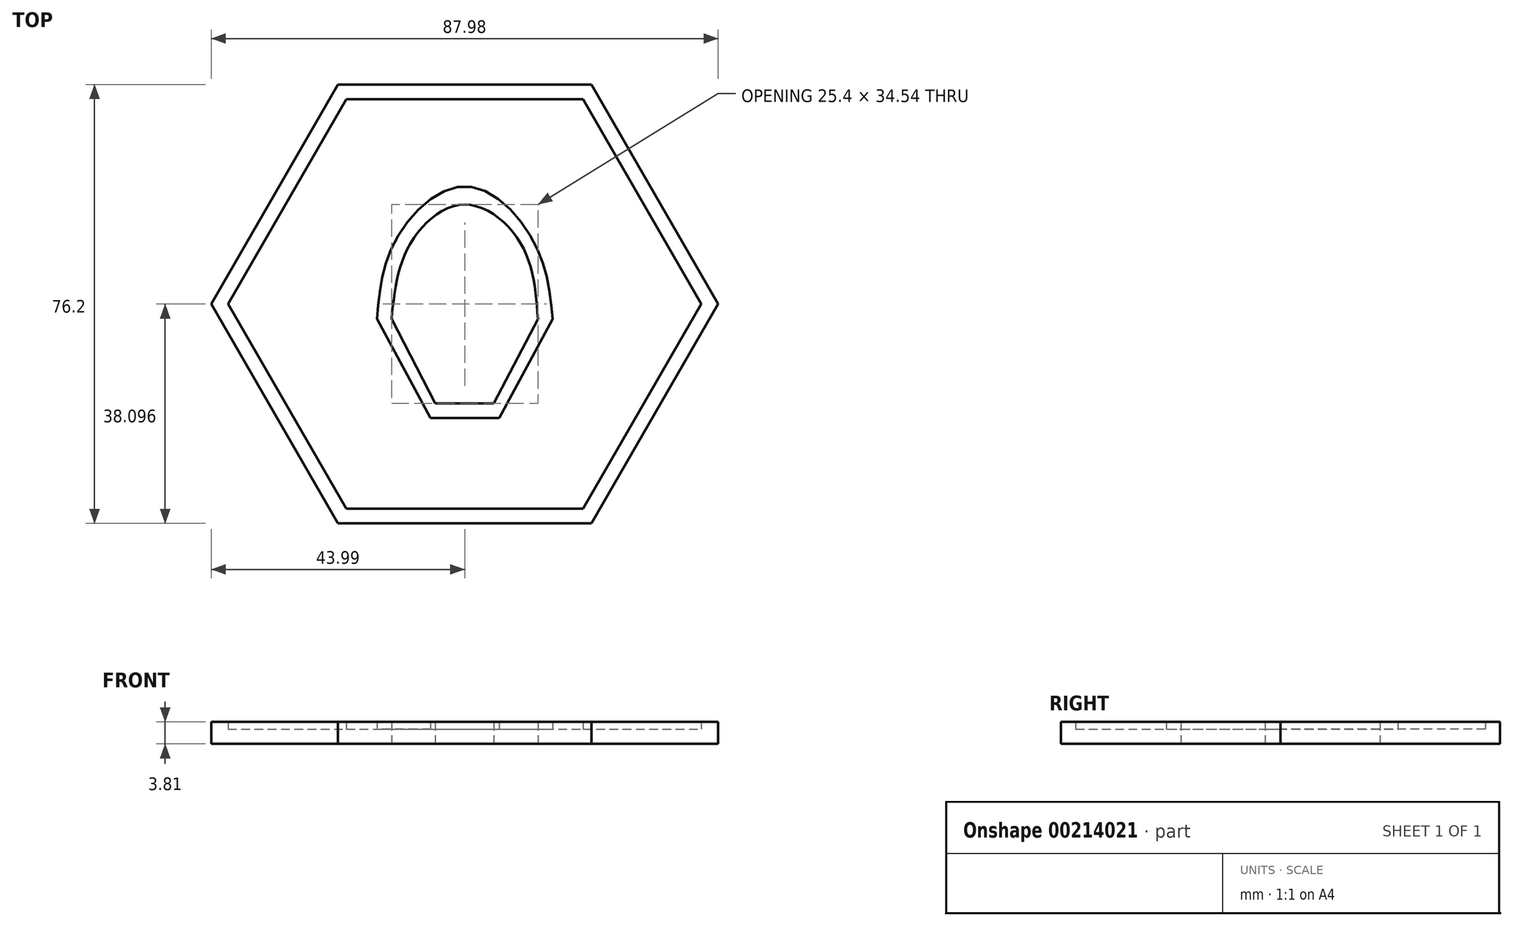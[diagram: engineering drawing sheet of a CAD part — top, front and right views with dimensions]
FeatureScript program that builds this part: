
annotation { "Feature Type Name" : "Feature", "Feature Type Description" : "" }
export const myFeature = defineFeature(function(context is Context, id is Id, definition is map)
    precondition{}
    {
        {
            var Q0;
            Q0=qCreatedBy(makeId("Top.planeOp"),FACE);
            var sketch = newSketch(context, id + "F0", { "sketchPlane" : qUnion([Q0])});
            skLineSegment(sketch, "E0", {"start": v(-12.7, 0) * mm, "end": v(12.7, 0) * mm});
            skLineSegment(sketch, "E1", {"start": v(0, -14.65) * mm, "end": v(0, 19.9) * mm});
            skLineSegment(sketch, "E2", {"start": v(-5.08, -14.65) * mm, "end": v(5.08, -14.65) * mm});
            skLineSegment(sketch, "E3", {"start": v(-5.08, -14.65) * mm, "end": v(-12.7, 0) * mm});
            skLineSegment(sketch, "E4", {"start": v(5.08, -14.65) * mm, "end": v(12.7, 0) * mm});
            skFitSpline(sketch, "E5", {"points": [v(-12.7, 0) * mm, v(-9.5, 13) * mm, v(0, 19.9) * mm, v(9.79, 13) * mm, v(12.7, 0) * mm], "startDerivative": vector(5.52, 52.75) * mm, "endDerivative": vector(3.81, -52.93) * mm});
            skCircle(sketch, "E6.cCircle", {"center": v(0, 2.63) * mm, "radius": 38.1 * mm, "construction": true});
            skLineSegment(sketch, "E6.0", {"start": v(22, 40.73) * mm, "end": v(44, 2.63) * mm});
            skLineSegment(sketch, "E6.1", {"start": v(44, 2.63) * mm, "end": v(22, -35.47) * mm});
            skLineSegment(sketch, "E6.2", {"start": v(22, -35.47) * mm, "end": v(-22, -35.47) * mm});
            skLineSegment(sketch, "E6.3", {"start": v(-22, -35.47) * mm, "end": v(-44, 2.63) * mm});
            skLineSegment(sketch, "E6.4", {"start": v(-44, 2.63) * mm, "end": v(-22, 40.73) * mm});
            skLineSegment(sketch, "E6.5", {"start": v(-22, 40.73) * mm, "end": v(22, 40.73) * mm});
            skPoint(sketch, "E6.0.midPoint", {"position": v(33, 21.68) * mm});
            skCircle(sketch, "E7.cCircle", {"center": v(0, 2.63) * mm, "radius": 35.56 * mm, "construction": true});
            skLineSegment(sketch, "E7.0", {"start": v(20.53, 38.19) * mm, "end": v(41.06, 2.63) * mm});
            skLineSegment(sketch, "E7.1", {"start": v(41.06, 2.63) * mm, "end": v(20.53, -32.93) * mm});
            skLineSegment(sketch, "E7.2", {"start": v(20.53, -32.93) * mm, "end": v(-20.53, -32.93) * mm});
            skLineSegment(sketch, "E7.3", {"start": v(-20.53, -32.93) * mm, "end": v(-41.06, 2.63) * mm});
            skLineSegment(sketch, "E7.4", {"start": v(-41.06, 2.63) * mm, "end": v(-20.53, 38.19) * mm});
            skLineSegment(sketch, "E7.5", {"start": v(-20.53, 38.19) * mm, "end": v(20.53, 38.19) * mm});
            skPoint(sketch, "E7.0.midPoint", {"position": v(30.8, 20.4) * mm});
            skLineSegment(sketch, "E8", {"start": v(-5.93, -17.19) * mm, "end": v(5.98, -17.19) * mm});
            skLineSegment(sketch, "E9", {"start": v(5.98, -17.19) * mm, "end": v(15.24, 0) * mm});
            skLineSegment(sketch, "E10", {"start": v(-5.93, -17.19) * mm, "end": v(-15.24, 0) * mm});
            skFitSpline(sketch, "E11", {"points": [v(-15.24, 0) * mm, v(-12.07, 13.56) * mm, v(0, 23.07) * mm, v(11.83, 13.75) * mm, v(15.24, 0) * mm], "startDerivative": vector(5.1, 55.52) * mm, "endDerivative": vector(4.63, -56.23) * mm});
            skSolve(sketch);
        }
        {
            var Q0;
            Q0=makeQuery(id+"F0.imprint","IMPRINT",FACE,{"disambiguationData":[TD([[makeQuery(id+"F0.imprint","IMPRINT",EDGE,{"derivedFrom":sQuery(id+"F0.wireOp",EDGE,"E7.0")}),-1.0]])]});
            extrude(context, id + "F1", {"entities" : qUnion([Q0]), "depth" : 2.54 * mm});
        }
        {
            var Q0;
            {var subQ1=sQuery(id+"F0.wireOp",EDGE,"E3");Q0=makeQuery(id+"F0.imprint","IMPRINT",FACE,{"disambiguationData":[TD([[makeQuery(id+"F0.imprint","IMPRINT",EDGE,{"derivedFrom":subQ1}),1.0]])]});}
            var Q1;
            Q1=makeQuery(id+"F0.imprint","IMPRINT",FACE,{"disambiguationData":[TD([[makeQuery(id+"F0.imprint","IMPRINT",EDGE,{"derivedFrom":sQuery(id+"F0.wireOp",EDGE,"E6.0")}),-1.0]])]});
            extrude(context, id + "F2", {"entities" : qUnion([Q0, Q1]), "operationType" : NewBodyOperationType.ADD, "depth" : 3.8 * mm});
        }
    });
